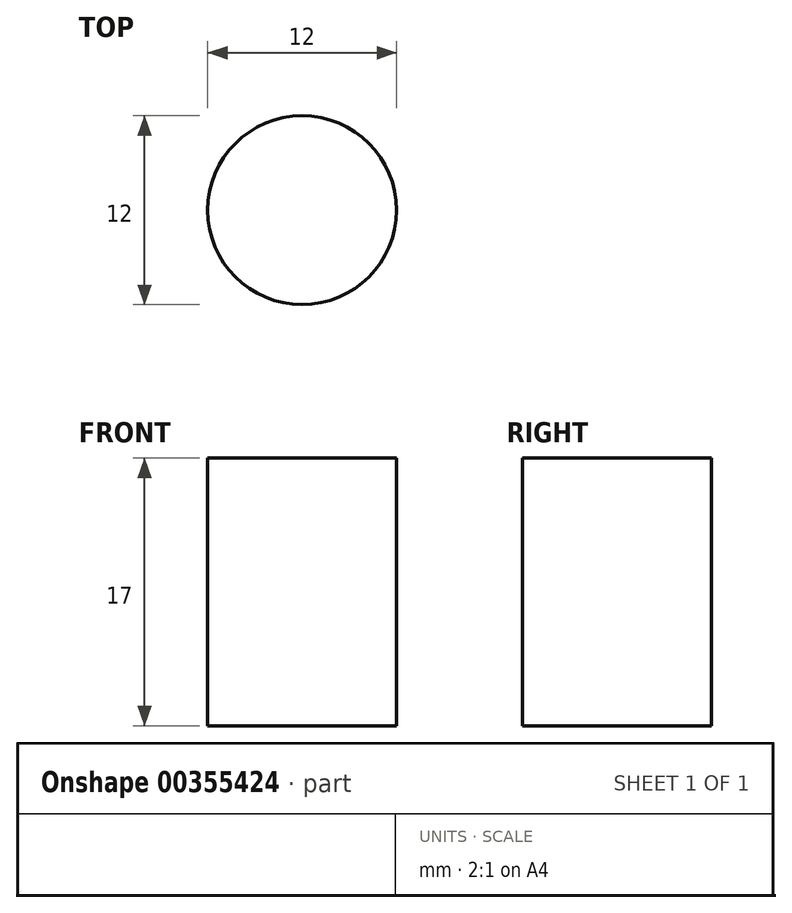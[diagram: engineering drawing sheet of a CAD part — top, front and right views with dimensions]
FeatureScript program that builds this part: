
annotation { "Feature Type Name" : "Feature", "Feature Type Description" : "" }
export const myFeature = defineFeature(function(context is Context, id is Id, definition is map)
    precondition{}
    {
        {
            var Q0;
            Q0=qCreatedBy(makeId("Top.planeOp"),FACE);
            var sketch = newSketch(context, id + "F0", { "sketchPlane" : qUnion([Q0])});
            skCircle(sketch, "E0", {"center": v(0, 0) * mm, "radius": 6 * mm});
            skSolve(sketch);
        }
        {
            var Q0;
            Q0 = qSketchRegion(id + "F0", true);
            extrude(context, id + "F1", {"entities" : qUnion([Q0]), "depth" : 17 * mm});
        }
    });
